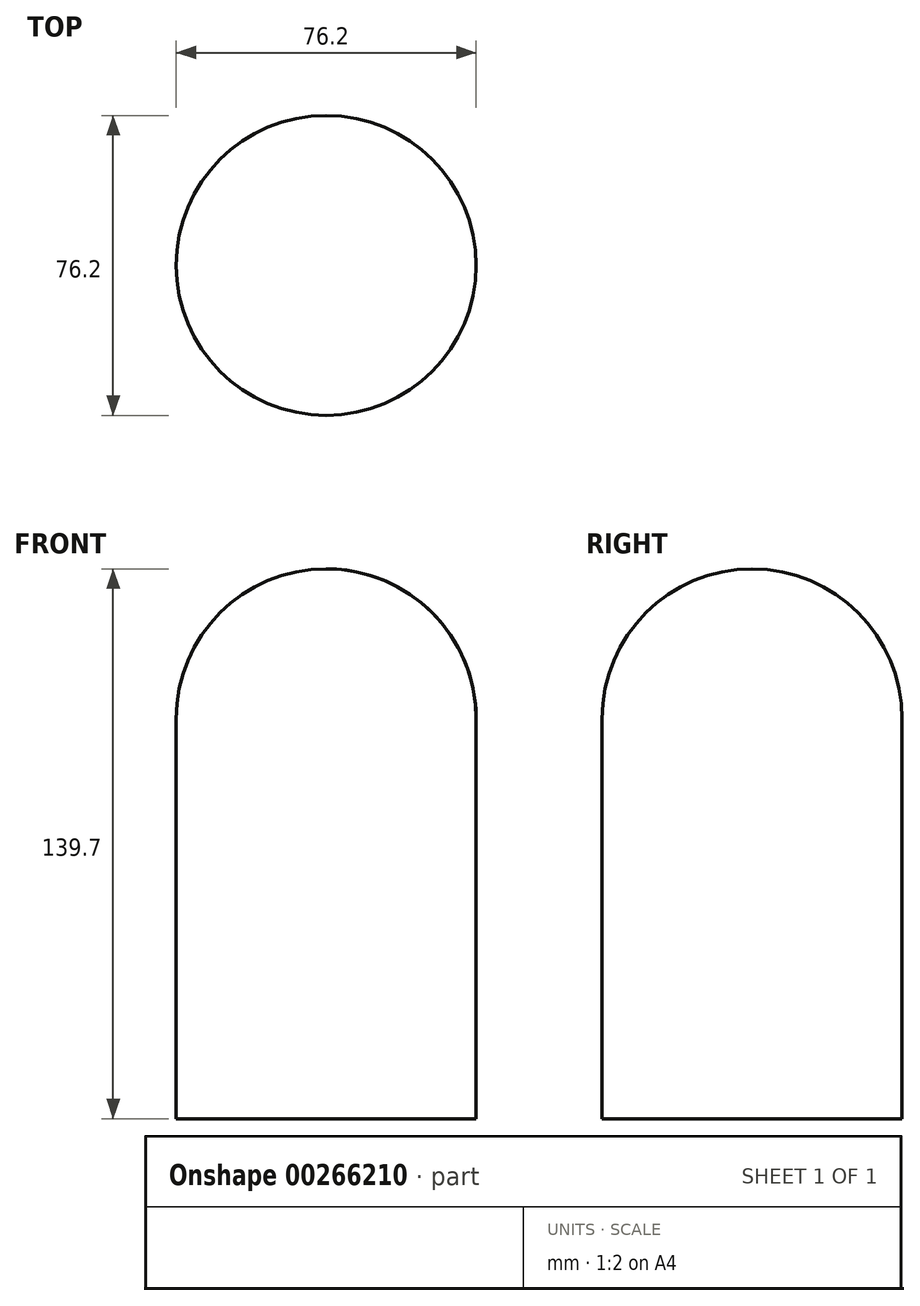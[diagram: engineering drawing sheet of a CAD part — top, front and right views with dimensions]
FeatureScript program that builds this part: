
annotation { "Feature Type Name" : "Feature", "Feature Type Description" : "" }
export const myFeature = defineFeature(function(context is Context, id is Id, definition is map)
    precondition{}
    {
        {
            var Q0;
            Q0=qCreatedBy(makeId("Front.planeOp"),FACE);
            var sketch = newSketch(context, id + "F0", { "sketchPlane" : qUnion([Q0])});
            skLineSegment(sketch, "E0", {"start": v(0, 0) * mm, "end": v(0, -101.6) * mm});
            skLineSegment(sketch, "E1", {"start": v(0, -101.6) * mm, "end": v(38.1, -101.6) * mm});
            skLineSegment(sketch, "E2", {"start": v(0, 0) * mm, "end": v(0, 38.1) * mm});
            skLineSegment(sketch, "E3", {"start": v(38.1, -101.6) * mm, "end": v(38.1, 0) * mm});
            skArc(sketch, "E4", {"start": v(38.1, 0) * mm, "mid": v(26.94, 26.94) * mm, "end": v(0, 38.1) * mm});
            skSolve(sketch);
        }
        {
            var Q0;
            Q0=makeQuery(id+"F0.imprint","IMPRINT",FACE,{"disambiguationData":[TD([[makeQuery(id+"F0.imprint","IMPRINT",EDGE,{"derivedFrom":sQuery(id+"F0.wireOp",EDGE,"E0")}),1.0]])]});
            var Q1;
            Q1=sQuery(id+"F0.wireOp",EDGE,"E2");
            revolve(context, id + "F1", {"entities" : qUnion([Q0]), "axis" : qUnion([Q1]), "revolveType" : RevolveType.FULL});
        }
    });
